# Revit family: EDFPVR320RC
name_source: partatom
category: Plumbing Fixtures
units: mm (PartAtom-declared; Revit-internal decimal feet)

## family parameters
Always vertical = Yes
Cut with Voids When Loaded = No
OmniClass Number = 23.45.00.00
OmniClass Title = Sanitary, Laundry, and Cleaning Equipment
Part Type = Normal
Room Calculation Point = No
Round Connector Dimension = Use Diameter
Shared = No
Work Plane-Based = No

## types (2) — shared parameters
Activation by = Mechanical Front Bubbler Button
Approx. Shipping Weight = 126 lbs
Assembly Code = D2010810
BODY_MATERIAL = WHT-White Granite Composite
BUBBLER_MATERIAL = Metal - Steel - Stainless - Chrome
BUTTON_MATERIAL = Metal - Steel - Stainless - Chrome
Bubbler Style = Vandal Resistant
CW Connection = Yes
Chilling Option = Non-refrigerated
DRAIN_MATERIAL = Metal - Steel - Stainless - Chrome
Description = Elkay Soft Sides Multi-Station Composite Fountain Non-Filtered Non-Refrigerated White Granite Composite
Dimensions (L x W x H) = 58 1/2inch x 18 1/16inch x 8Inch
Drain_Pipe 1 1/2" = 25 mm  [stored 0.082021 ft]
Finish = White Granite Composite (WHT)
HW Connection = No
Inlet_Pipe = 10 mm  [stored 0.0328084 ft]
Installation Location = Indoor + Outdoor
Manufacturer = Elkay
Mounting Type = Wall Mount (On Wall)
No. of Stations Served = 3
Power = No Electrical Required
SINK_MATERIAL = Metal - Steel - Stainless - Chrome
Vent Connection = No
Version = 1.0.0.0
Waste Connection = Yes

## type names (no varying parameters)
- EDFPVR320RC
- EDFPVR320RFPK

note: column(s) folded — value = type name in every type: Model

note: [stored X ft] marks values corroborated as IEEE doubles in the binary element streams (Revit-internal decimal feet)

## geometry (parser evidence)
native form markers: Sweep x13
no freeform markers — native parametric forms only
